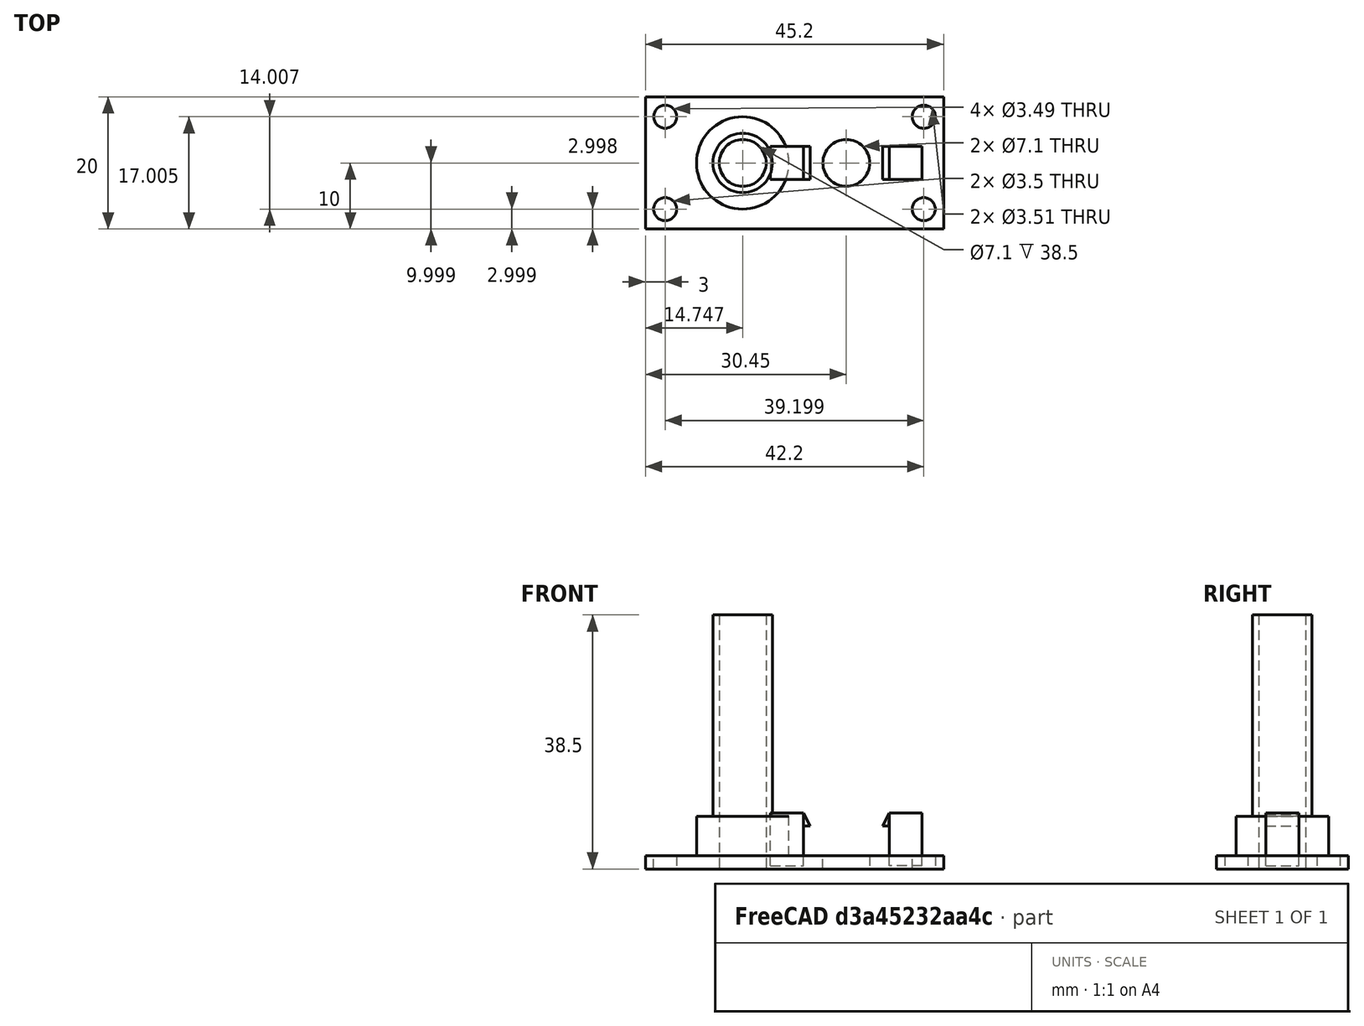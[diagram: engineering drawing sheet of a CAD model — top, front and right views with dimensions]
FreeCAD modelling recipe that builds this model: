
FCSTD DOCUMENT  (FreeCAD 0.17R13522 (Git))
Label: base_media_con_agujeros
License: CreativeCommons Attribution-ShareAlike
LicenseURL: http://creativecommons.org/licenses/by-sa/4.0/
objects: Part::Part2DObjectPython×11, Part::Extrusion×9, Part::Cut×7, Part::Feature×3, Part::Box×1, Part::MultiFuse×1
note: 32 computed .brp shape members not serialized (recipe doc carries the construction recipe); baked Part::Feature solids carry a one-line shape summary decoded from their .brp

FEATURE [Part::Box] Box  label="placa base"
  AttacherType = Attacher::AttachEngine3D
  Height = 2
  Length = 45.2
  Width = 20
FEATURE [Part::Part2DObjectPython] Circle  label="taladro inferior izquierdo"  # Draft 2D object (typed FeaturePython)
  FirstAngle = 0
  LastAngle = 0
  MakeFace = false
  Placement = pos=(3,2.99873,2) rot=(0,0,1;3.14159rad)
  Radius = 1.74945
FEATURE [Part::Part2DObjectPython] Circle001  label="taladro inferior derecho"  # Draft 2D object (typed FeaturePython)
  FirstAngle = 0
  LastAngle = 0
  MakeFace = false
  Placement = pos=(42.1991,2.99781,2) rot=(0,0,1;3.14159rad)
  Radius = 1.7464
FEATURE [Part::Part2DObjectPython] Circle002  label="taladro superior derecho"  # Draft 2D object (typed FeaturePython)
  FirstAngle = 0
  LastAngle = 0
  MakeFace = false
  Placement = pos=(42.2,17.005,2) rot=(0,0,1;3.14159rad)
  Radius = 1.75369
FEATURE [Part::Part2DObjectPython] Circle003  label="taladro superior izquierdo"  # Draft 2D object (typed FeaturePython)
  FirstAngle = 0
  LastAngle = 0
  MakeFace = false
  Placement = pos=(3,17.005,2) rot=(0,0,1;3.14159rad)
  Radius = 1.74699
FEATURE [Part::Extrusion] Extrude
  Base = -> Circle003
  Dir = (0,0,1)
  DirMode = 2
  FaceMakerClass = Part::FaceMakerBullseye
  LengthFwd = 10
  LengthRev = 0
  Placement = pos=(0,0,-5) rot=(0,0,1;0rad)
  Solid = true
  Symmetric = false
FEATURE [Part::Extrusion] Extrude001
  Base = -> Circle
  Dir = (0,0,1)
  DirMode = 2
  FaceMakerClass = Part::FaceMakerBullseye
  LengthFwd = 10
  LengthRev = 0
  Placement = pos=(0,0,-5) rot=(0,0,1;0rad)
  Solid = true
  Symmetric = false
FEATURE [Part::Extrusion] Extrude002
  Base = -> Circle001
  Dir = (0,0,1)
  DirMode = 2
  FaceMakerClass = Part::FaceMakerBullseye
  LengthFwd = 10
  LengthRev = 0
  Placement = pos=(0,0,-5) rot=(0,0,1;0rad)
  Solid = true
  Symmetric = false
FEATURE [Part::Extrusion] Extrude003
  Base = -> Circle002
  Dir = (0,0,1)
  DirMode = 2
  FaceMakerClass = Part::FaceMakerBullseye
  LengthFwd = 10
  LengthRev = 0
  Placement = pos=(0,0,-5) rot=(0,0,1;0rad)
  Solid = true
  Symmetric = false
FEATURE [Part::Cut] Cut
  Base = -> Box
  Refine = true
  Tool = -> Extrude001
FEATURE [Part::Cut] Cut001
  Base = -> Cut
  Refine = true
  Tool = -> Extrude
FEATURE [Part::Cut] Cut002
  Base = -> Cut001
  Refine = true
  Tool = -> Extrude002
FEATURE [Part::Cut] Cut003  label="base con taladros en esquina"
  Base = -> Cut002
  Refine = true
  Tool = -> Extrude003
FEATURE [Part::Part2DObjectPython] Circle004  # Draft 2D object (typed FeaturePython)
  FirstAngle = 0
  LastAngle = 0
  MakeFace = false
  Placement = pos=(30.45,10,2) rot=(0,0,1;3.14159rad)
  Radius = 3.55
FEATURE [Part::Extrusion] Extrude004
  Base = -> Circle004
  Dir = (0,0,1)
  DirMode = 2
  FaceMakerClass = Part::FaceMakerBullseye
  LengthFwd = 10
  LengthRev = 0
  Placement = pos=(0,0,-4) rot=(0,0,1;0rad)
  Solid = true
  Symmetric = false
FEATURE [Part::Cut] Cut004  label="base con agujeros"
  Base = -> Cut003
  Refine = true
  Tool = -> Extrude004
FEATURE [Part::Part2DObjectPython] Rectangle  # Draft 2D object (typed FeaturePython)
  ChamferSize = 0
  Columns = 1
  FilletRadius = 0
  Height = 5
  Length = 5
  MakeFace = false
  Placement = pos=(23.95,12.5,2) rot=(0,0,1;3.14159rad)
  Rows = 1
FEATURE [Part::Part2DObjectPython] Rectangle001  # Draft 2D object (typed FeaturePython)
  ChamferSize = 0
  Columns = 1
  FilletRadius = 0
  Height = 5
  Length = -5
  MakeFace = false
  Placement = pos=(36.95,12.5,2) rot=(0,0,1;3.14159rad)
  Rows = 1
FEATURE [Part::Feature] Cut004_solid001001  label="base con agujeros (Solid)002"
  shape: bbox 45.2 x 20 x 2 mm, 11 faces (baked)
FEATURE [Part::Part2DObjectPython] Circle005  # Draft 2D object (typed FeaturePython)
  FirstAngle = 0
  LastAngle = 0
  MakeFace = false
  Placement = pos=(14.7474,9.99931,2) rot=(0,0,1;0rad)
  Radius = 3.55
FEATURE [Part::Part2DObjectPython] Circle006  # Draft 2D object (typed FeaturePython)
  FirstAngle = 0
  LastAngle = 0
  MakeFace = false
  Placement = pos=(14.7474,9.99931,2) rot=(0,0,1;0rad)
  Radius = 4.5
  Support = -> [Cut004_solid001001]
FEATURE [Part::Part2DObjectPython] Circle007  # Draft 2D object (typed FeaturePython)
  FirstAngle = 0
  LastAngle = 0
  MakeFace = false
  Placement = pos=(14.7474,9.99931,2) rot=(0,0,1;0rad)
  Radius = 7
FEATURE [Part::Extrusion] Extrude005
  Base = -> Circle005
  Dir = (0,0,1)
  DirMode = 2
  FaceMakerClass = Part::FaceMakerBullseye
  LengthFwd = 50
  LengthRev = 0
  Solid = true
  Symmetric = false
FEATURE [Part::Extrusion] Extrude006
  Base = -> Circle006
  Dir = (0,0,1)
  DirMode = 2
  FaceMakerClass = Part::FaceMakerBullseye
  LengthFwd = 36.5
  LengthRev = 0
  Solid = true
  Symmetric = false
FEATURE [Part::Extrusion] Extrude007
  Base = -> Circle007
  Dir = (0,0,1)
  DirMode = 2
  FaceMakerClass = Part::FaceMakerBullseye
  LengthFwd = 6
  LengthRev = 0
  Solid = true
  Symmetric = false
FEATURE [Part::MultiFuse] Fusion
  Refine = true
  Shapes = -> [Cut004_solid001001,Extrude007,Extrude006]
FEATURE [Part::Cut] Cut005
  Base = -> Fusion
  Refine = true
  Tool = -> Extrude005
FEATURE [Part::Part2DObjectPython] Circle008  # Draft 2D object (typed FeaturePython)
  FirstAngle = 0
  LastAngle = 0
  MakeFace = false
  Placement = pos=(14.7474,9.99931,2) rot=(0,0,1;0rad)
  Radius = 3.55
FEATURE [Part::Extrusion] Extrude008
  Base = -> Circle008
  Dir = (0,0,1)
  DirMode = 2
  FaceMakerClass = Part::FaceMakerBullseye
  LengthFwd = 20
  LengthRev = 0
  Placement = pos=(0,0,-8) rot=(0,0,1;0rad)
  Solid = true
  Symmetric = false
FEATURE [Part::Cut] Cut006
  Base = -> Cut005
  Refine = true
  Tool = -> Extrude008
FEATURE [Part::Feature] Clone002
  Placement = pos=(22.6,10,-1.5) rot=(0,0,1;0rad)
  shape: bbox 6 x 5 x 8 mm, 10 faces (baked)
FEATURE [Part::Feature] Clone001001  label="Clone003"
  Placement = pos=(38.3,10,9.927e-05) rot=(0,0,1;0rad)
  shape: bbox 6 x 5 x 8 mm, 10 faces (baked)
